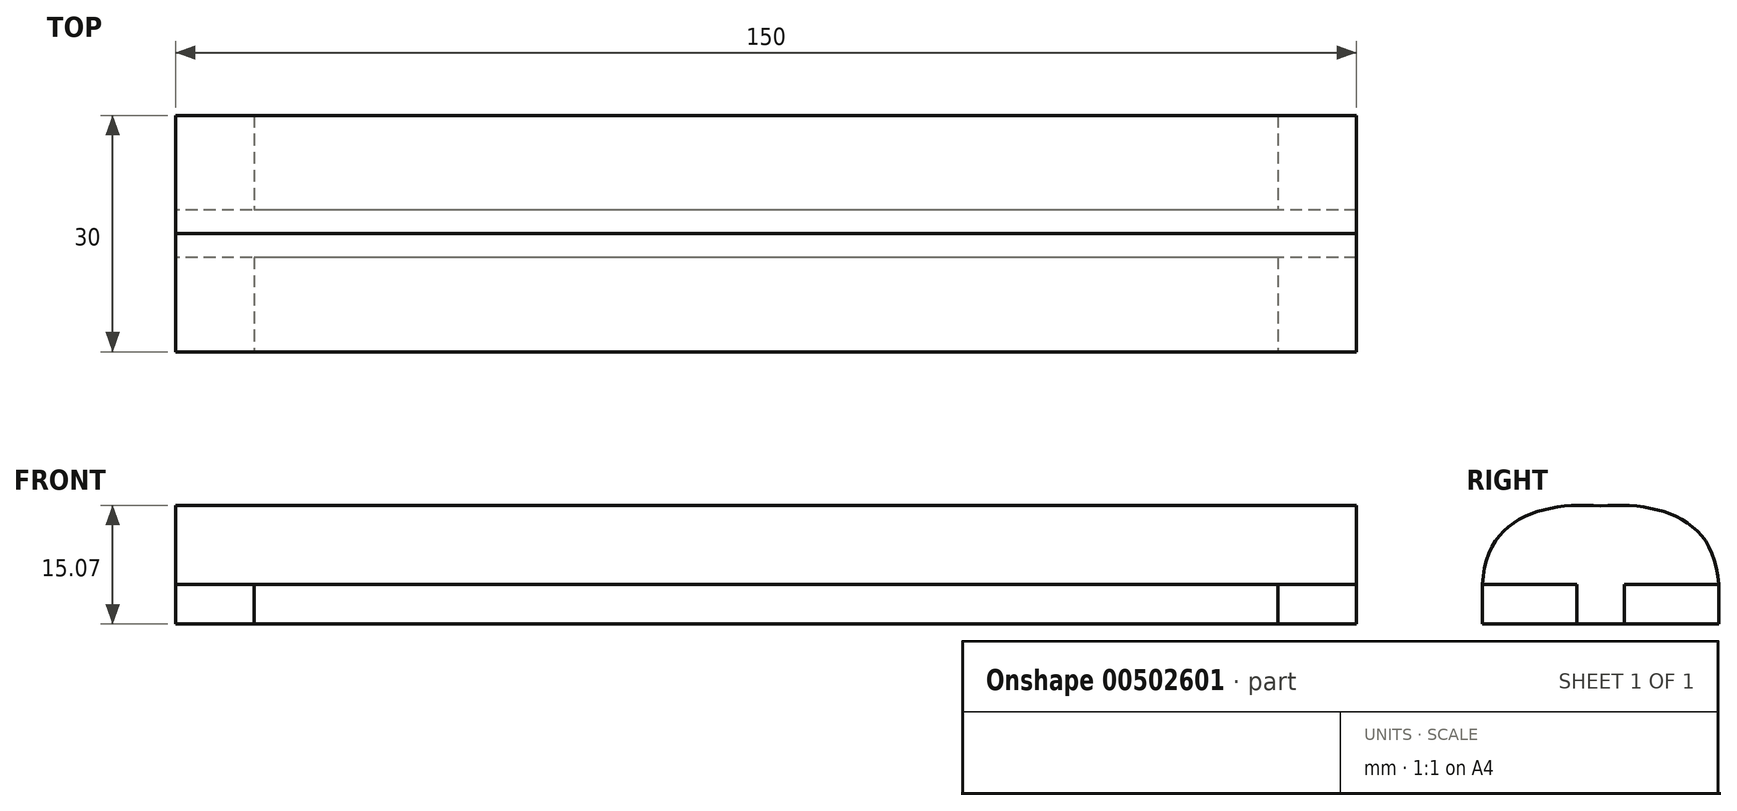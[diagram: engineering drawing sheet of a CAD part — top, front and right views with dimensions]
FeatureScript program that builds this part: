
annotation { "Feature Type Name" : "Feature", "Feature Type Description" : "" }
export const myFeature = defineFeature(function(context is Context, id is Id, definition is map)
    precondition{}
    {
        {
            var Q0;
            Q0=qCreatedBy(makeId("Right.planeOp"),FACE);
            var sketch = newSketch(context, id + "F0", { "sketchPlane" : qUnion([Q0])});
            skLineSegment(sketch, "E0", {"start": v(-3, -5) * mm, "end": v(0, -5) * mm});
            skLineSegment(sketch, "E1", {"start": v(-3, -5) * mm, "end": v(-3, 0) * mm});
            skLineSegment(sketch, "E2", {"start": v(-3, 0) * mm, "end": v(-15, 0) * mm});
            skFitSpline(sketch, "E3", {"points": [v(-15, 0) * mm, v(0, 10) * mm], "startDerivative": vector(1.33, 26.31) * mm, "endDerivative": vector(21.19, -1.44) * mm});
            skLineSegment(sketch, "E4", {"start": v(0, 10) * mm, "end": v(0, -5) * mm});
            skLineSegment(sketch, "E5", {"start": v(-15, 0) * mm, "end": v(-15, -5) * mm});
            skLineSegment(sketch, "E6", {"start": v(-15, -5) * mm, "end": v(-3, -5) * mm});
            skLineSegment(sketch, "E7.MirrorCS", {"start": v(3, -5) * mm, "end": v(0, -5) * mm});
            skFitSpline(sketch, "E8.MirrorCS", {"points": [v(15, 0) * mm, v(0, 10) * mm], "startDerivative": vector(-1.33, 26.31) * mm, "endDerivative": vector(-21.19, -1.44) * mm});
            skLineSegment(sketch, "E9.MirrorCS", {"start": v(15, -5) * mm, "end": v(3, -5) * mm});
            skLineSegment(sketch, "E10.MirrorCS", {"start": v(3, 0) * mm, "end": v(15, 0) * mm});
            skLineSegment(sketch, "E11.MirrorCS", {"start": v(3, -5) * mm, "end": v(3, 0) * mm});
            skLineSegment(sketch, "E12.MirrorCS", {"start": v(15, 0) * mm, "end": v(15, -5) * mm});
            skSolve(sketch);
        }
        {
            var Q0;
            Q0=makeQuery(id+"F0.imprint","IMPRINT",FACE,{"disambiguationData":[TD([[makeQuery(id+"F0.imprint","IMPRINT",EDGE,{"derivedFrom":sQuery(id+"F0.wireOp",EDGE,"E1")}),1.0]])]});
            var Q1;
            Q1=makeQuery(id+"F0.imprint","IMPRINT",FACE,{"disambiguationData":[TD([[makeQuery(id+"F0.imprint","IMPRINT",EDGE,{"derivedFrom":sQuery(id+"F0.wireOp",EDGE,"E9.MirrorCS")}),-1.0]])]});
            extrude(context, id + "F1", {"entities" : qUnion([Q0, Q1]), "endBound" : BoundingType.SYMMETRIC, "depth" : 130 * mm});
        }
        {
            var Q0;
            Q0=makeQuery(id+"F0.imprint","IMPRINT",FACE,{"disambiguationData":[TD([[makeQuery(id+"F0.imprint","IMPRINT",EDGE,{"derivedFrom":sQuery(id+"F0.wireOp",EDGE,"E0")}),1.0]])]});
            var Q1;
            Q1=makeQuery(id+"F0.imprint","IMPRINT",FACE,{"disambiguationData":[TD([[makeQuery(id+"F0.imprint","IMPRINT",EDGE,{"derivedFrom":sQuery(id+"F0.wireOp",EDGE,"E4")}),1.0]])]});
            extrude(context, id + "F2", {"entities" : qUnion([Q0, Q1]), "endBound" : BoundingType.SYMMETRIC, "depth" : 150 * mm});
        }
    });
